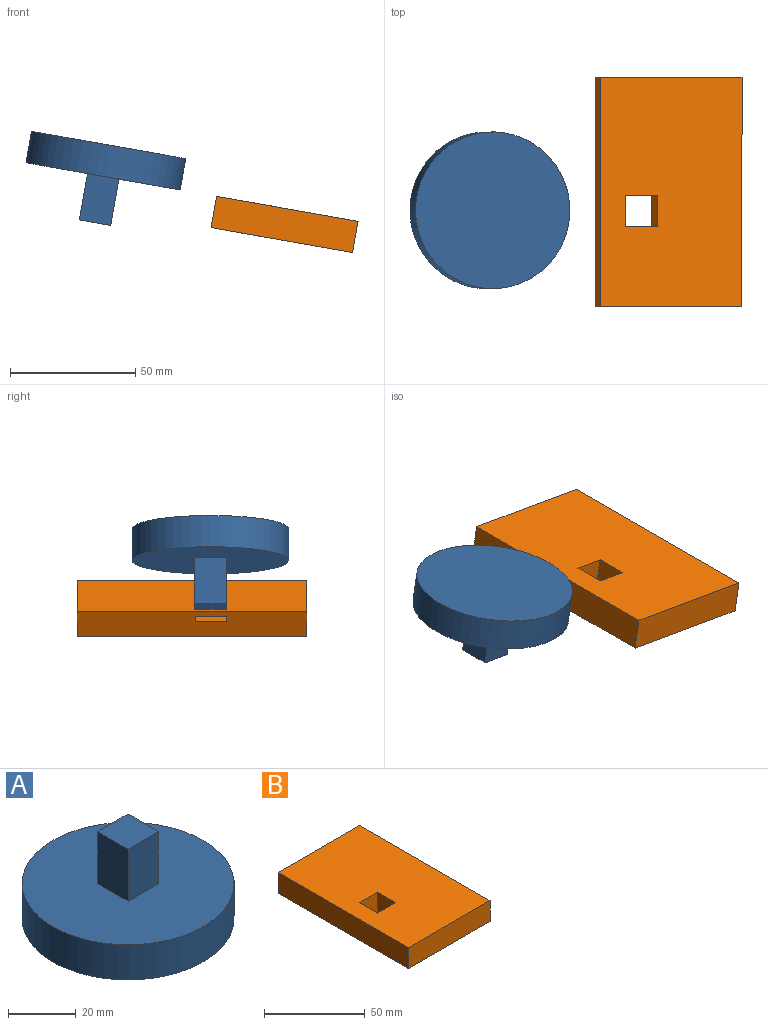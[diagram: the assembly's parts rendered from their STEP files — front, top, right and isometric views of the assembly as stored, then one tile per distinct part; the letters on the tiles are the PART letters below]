
ASSEMBLY  parts=2 mates=1
PART A: 8 faces, bbox 62.6x62.6x31.5 mm
  f0: plane 62.63x62.63mm, normal (0,0,1), area 2919.4mm2, adj f1,f3,f4,f5,f6
  f1: cylinder r=31.31mm len=62.63mm, axis (0,0,-1), area 2498.8mm2, adj f0,f2
  f2: plane 62.63x62.63mm, normal (0,0,-1), area 3080.7mm2, adj f1
  f3: plane 18.8x12.7mm, normal (-1,0,0), area 238.7mm2, adj f0,f4,f6,f7
  f4: plane 18.8x12.7mm, normal (0,-1,0), area 238.7mm2, adj f0,f3,f5,f7
  f5: plane 18.8x12.7mm, normal (1,0,0), area 238.7mm2, adj f0,f4,f6,f7
  f6: plane 18.8x12.7mm, normal (0,1,0), area 238.7mm2, adj f0,f3,f5,f7
  f7: plane 12.7x12.7mm, normal (0,0,1), area 161.3mm2, adj f3,f4,f5,f6
PART B: 10 faces, bbox 57.4x91.7x12.7 mm
  f0: plane 91.66x12.7mm, normal (1,0,0), area 1164.1mm2, adj f1,f3,f4,f5
  f1: plane 57.37x12.7mm, normal (0,1,0), area 728.5mm2, adj f0,f2,f4,f5
  f2: plane 91.66x12.7mm, normal (-1,0,0), area 1164.1mm2, adj f1,f3,f4,f5
  f3: plane 57.37x12.7mm, normal (0,-1,0), area 728.5mm2, adj f0,f2,f4,f5
  f4: plane 91.66x57.37mm, normal (0,0,1), area 5097.1mm2, adj f0,f1,f2,f3,f6,f7,f8,f9
  f5: plane 91.66x57.37mm, normal (0,0,-1), area 5097.1mm2, adj f0,f1,f2,f3,f6,f7,f8,f9
  f6: plane 12.7x12.7mm, normal (-1,0,0), area 161.3mm2, adj f4,f5,f7,f8
  f7: plane 12.7x12.7mm, normal (0,1,0), area 161.3mm2, adj f4,f5,f6,f9
  f8: plane 12.7x12.7mm, normal (0,-1,0), area 161.3mm2, adj f4,f5,f6,f9
  f9: plane 12.7x12.7mm, normal (1,0,0), area 161.3mm2, adj f4,f5,f7,f8
PLACE A rot(axis=(0,-1,0),170deg) t=(-275.62,-23.23,58.49)mm
PLACE B rot(axis=(0,1,0),10deg) t=(22.31,-12.75,-19.83)mm
MATE planar A.f1 <-> B.f4  axis (-0.17,0,-0.98) through (-165.72,-56.97,26.22)mm
